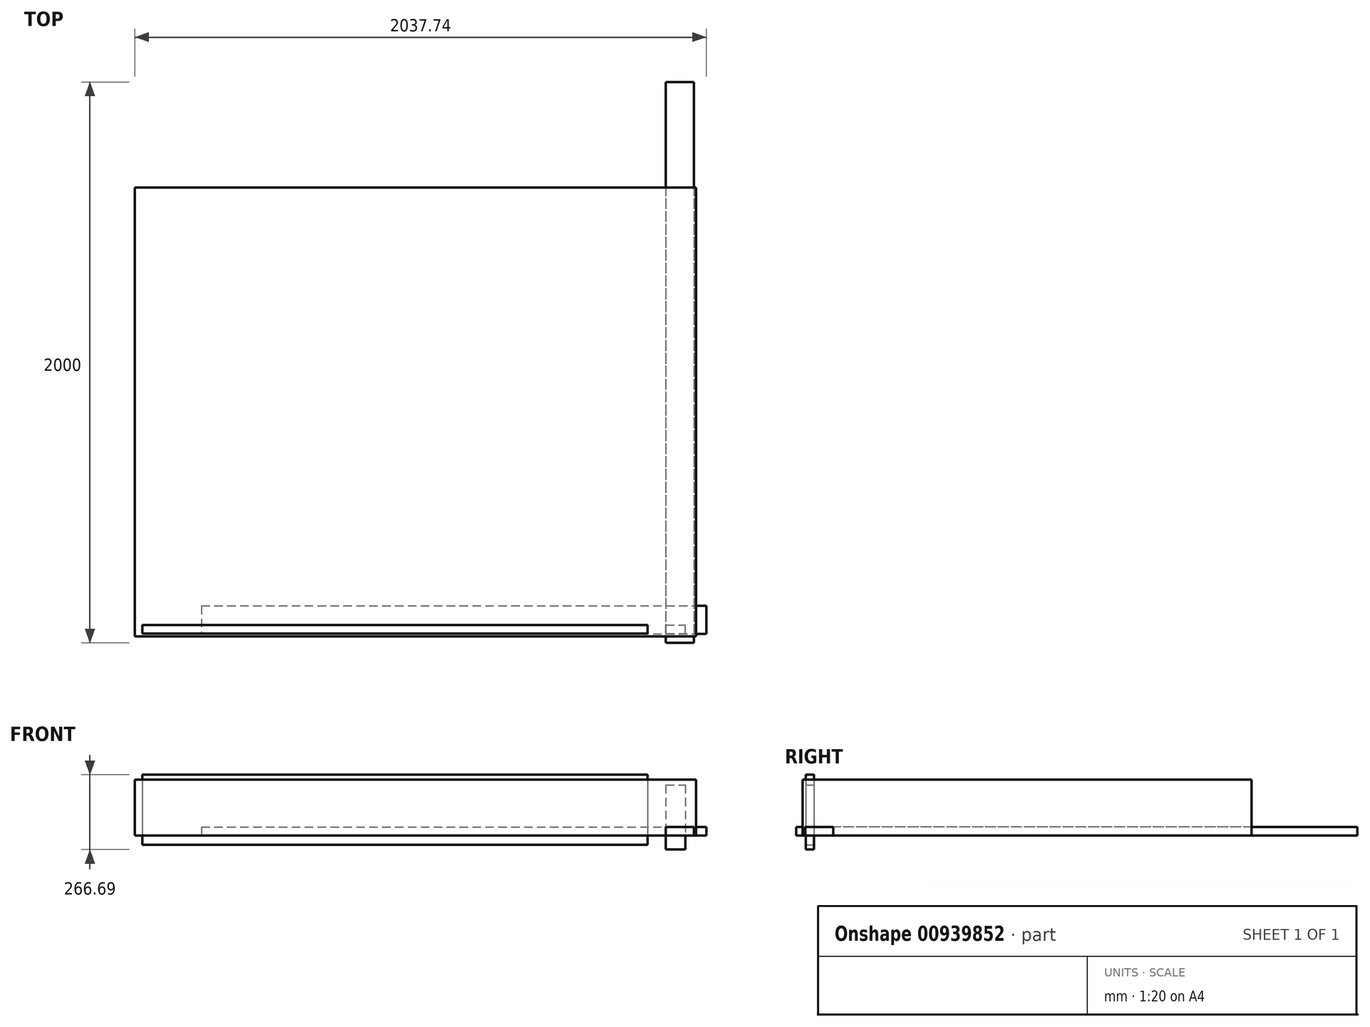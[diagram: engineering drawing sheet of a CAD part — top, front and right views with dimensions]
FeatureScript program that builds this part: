
annotation { "Feature Type Name" : "Feature", "Feature Type Description" : "" }
export const myFeature = defineFeature(function(context is Context, id is Id, definition is map)
    precondition{}
    {
        {
            var Q0;
            Q0=qCreatedBy(makeId("Front.planeOp"),FACE);
            var sketch = newSketch(context, id + "F0", { "sketchPlane" : qUnion([Q0])});
            skLineSegment(sketch, "E0.bottom", {"start": v(-1914.26, 216.7) * mm, "end": v(-114.26, 216.7) * mm});
            skLineSegment(sketch, "E0.top", {"start": v(-1914.26, -33.3) * mm, "end": v(-114.26, -33.3) * mm});
            skLineSegment(sketch, "E0.left", {"start": v(-1914.26, 216.7) * mm, "end": v(-1914.26, -33.3) * mm});
            skLineSegment(sketch, "E0.right", {"start": v(-114.26, 216.7) * mm, "end": v(-114.26, -33.3) * mm});
            skSolve(sketch);
        }
        {
            var Q0;
            Q0=qSketchRegion(id+"F0",true);
            extrude(context, id + "F1", {"entities" : qUnion([Q0]), "depth" : 30 * mm, "offsetDistance" : 25 * mm});
        }
        {
            var Q0;
            Q0=qCreatedBy(makeId("Top.planeOp"),FACE);
            var sketch = newSketch(context, id + "F2", { "sketchPlane" : qUnion([Q0])});
            skLineSegment(sketch, "E1.bottom", {"start": v(-49.26, 1936.58) * mm, "end": v(50.74, 1936.58) * mm});
            skLineSegment(sketch, "E1.top", {"start": v(-49.26, -63.42) * mm, "end": v(50.74, -63.42) * mm});
            skLineSegment(sketch, "E1.left", {"start": v(-49.26, 1936.58) * mm, "end": v(-49.26, -63.42) * mm});
            skLineSegment(sketch, "E1.right", {"start": v(50.74, 1936.58) * mm, "end": v(50.74, -63.42) * mm});
            skSolve(sketch);
        }
        {
            var Q0;
            Q0=qSketchRegion(id+"F2",true);
            extrude(context, id + "F3", {"entities" : qUnion([Q0]), "depth" : 30 * mm, "offsetDistance" : 25 * mm});
        }
        {
            var Q0;
            Q0=qCreatedBy(makeId("Front.planeOp"),FACE);
            var sketch = newSketch(context, id + "F4", { "sketchPlane" : qUnion([Q0])});
            skLineSegment(sketch, "E2.bottom", {"start": v(-49.26, 180.01) * mm, "end": v(20.74, 180.01) * mm});
            skLineSegment(sketch, "E2.top", {"start": v(-49.26, -49.99) * mm, "end": v(20.74, -49.99) * mm});
            skLineSegment(sketch, "E2.left", {"start": v(-49.26, 180.01) * mm, "end": v(-49.26, -49.99) * mm});
            skLineSegment(sketch, "E2.right", {"start": v(20.74, 180.01) * mm, "end": v(20.74, -49.99) * mm});
            skSolve(sketch);
        }
        {
            var Q0;
            Q0=qSketchRegion(id+"F4",true);
            extrude(context, id + "F5", {"entities" : qUnion([Q0]), "depth" : 30 * mm, "offsetDistance" : 25 * mm});
        }
        {
            var Q0;
            Q0=qCreatedBy(makeId("Top.planeOp"),FACE);
            var sketch = newSketch(context, id + "F6", { "sketchPlane" : qUnion([Q0])});
            skLineSegment(sketch, "E3.bottom", {"start": v(-1941.66, 1559.63) * mm, "end": v(58.34, 1559.63) * mm});
            skLineSegment(sketch, "E3.top", {"start": v(-1941.66, -40.37) * mm, "end": v(58.34, -40.37) * mm});
            skLineSegment(sketch, "E3.left", {"start": v(-1941.66, 1559.63) * mm, "end": v(-1941.66, -40.37) * mm});
            skLineSegment(sketch, "E3.right", {"start": v(58.34, 1559.63) * mm, "end": v(58.34, -40.37) * mm});
            skSolve(sketch);
        }
        {
            var Q0;
            Q0=qSketchRegion(id+"F6",true);
            extrude(context, id + "F7", {"entities" : qUnion([Q0]), "depth" : 200 * mm, "offsetDistance" : 25 * mm});
        }
        {
            var Q0;
            Q0=qCreatedBy(makeId("Top.planeOp"),FACE);
            var sketch = newSketch(context, id + "F8", { "sketchPlane" : qUnion([Q0])});
            skLineSegment(sketch, "E4.bottom", {"start": v(-1703.92, 68.52) * mm, "end": v(96.08, 68.52) * mm});
            skLineSegment(sketch, "E4.top", {"start": v(-1703.92, -31.48) * mm, "end": v(96.08, -31.48) * mm});
            skLineSegment(sketch, "E4.left", {"start": v(-1703.92, 68.52) * mm, "end": v(-1703.92, -31.48) * mm});
            skLineSegment(sketch, "E4.right", {"start": v(96.08, 68.52) * mm, "end": v(96.08, -31.48) * mm});
            skSolve(sketch);
        }
        {
            var Q0;
            Q0=qSketchRegion(id+"F8",true);
            extrude(context, id + "F9", {"entities" : qUnion([Q0]), "depth" : 30 * mm, "offsetDistance" : 25 * mm});
        }
    });
